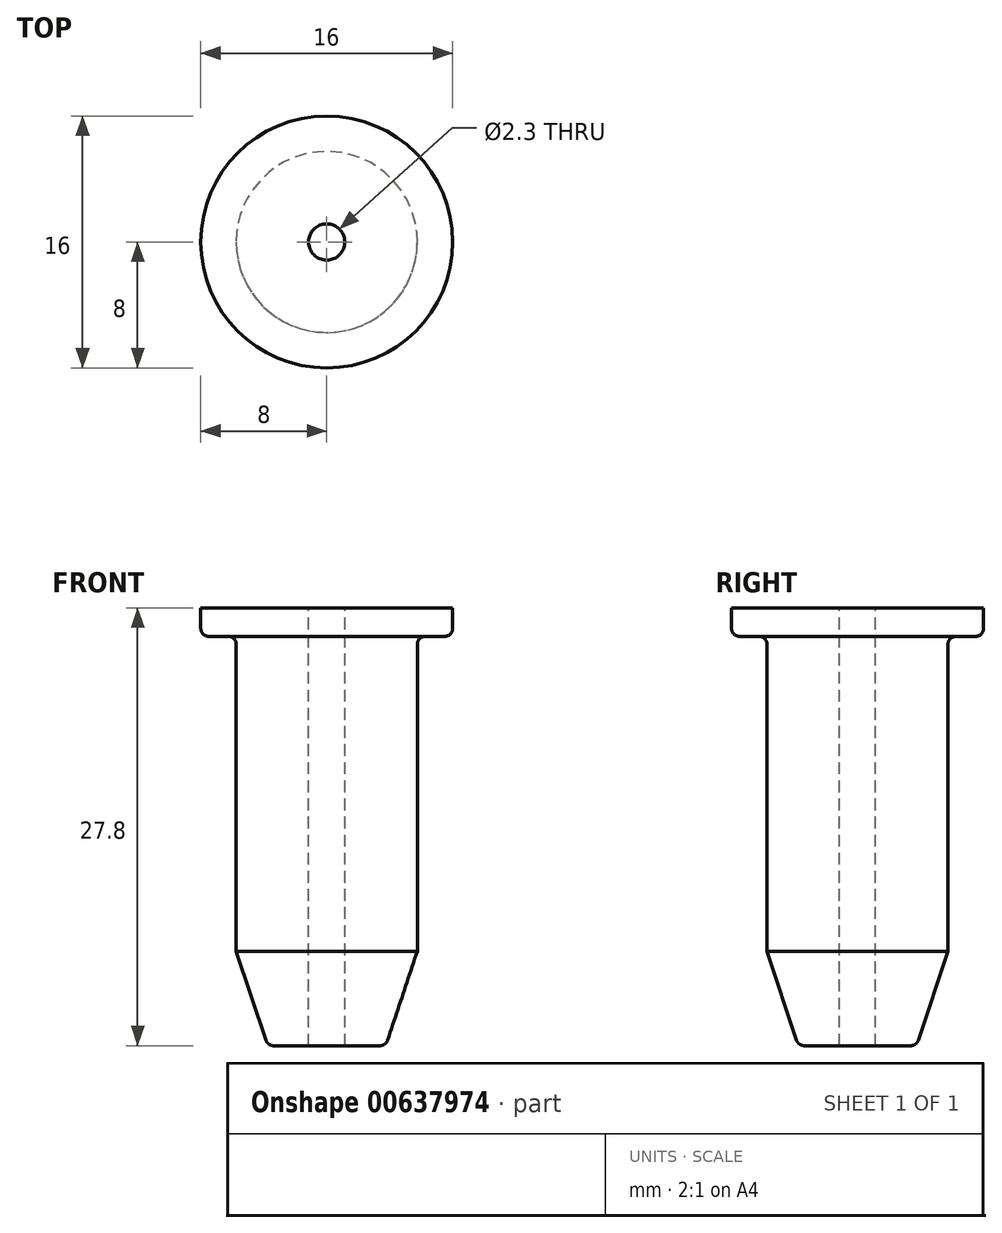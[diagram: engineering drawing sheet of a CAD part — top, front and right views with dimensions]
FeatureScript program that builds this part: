
annotation { "Feature Type Name" : "Feature", "Feature Type Description" : "" }
export const myFeature = defineFeature(function(context is Context, id is Id, definition is map)
    precondition{}
    {
        {
            var Q0;
            Q0=qCreatedBy(makeId("Front.planeOp"),FACE);
            var sketch = newSketch(context, id + "F0", { "sketchPlane" : qUnion([Q0])});
            skLineSegment(sketch, "E0", {"start": v(0, 27.8) * mm, "end": v(8, 27.8) * mm});
            skLineSegment(sketch, "E1", {"start": v(8, 27.8) * mm, "end": v(8, 26) * mm});
            skLineSegment(sketch, "E2", {"start": v(8, 26) * mm, "end": v(5.75, 26) * mm});
            skLineSegment(sketch, "E3", {"start": v(5.75, 26) * mm, "end": v(5.75, 0) * mm});
            skLineSegment(sketch, "E4", {"start": v(0, 27.8) * mm, "end": v(0, 0) * mm});
            skLineSegment(sketch, "E5", {"start": v(0, 0) * mm, "end": v(5.75, 0) * mm});
            skSolve(sketch);
        }
        {
            var Q0;
            Q0=makeQuery(id+"F0.imprint","IMPRINT",FACE,{"disambiguationData":[TD([[makeQuery(id+"F0.imprint","IMPRINT",EDGE,{"derivedFrom":sQuery(id+"F0.wireOp",EDGE,"E0")}),-1.0]])]});
            var Q1;
            Q1=sQuery(id+"F0.wireOp",EDGE,"E4");
            revolve(context, id + "F1", {"entities" : qUnion([Q0]), "axis" : qUnion([Q1]), "revolveType" : RevolveType.FULL});
        }
        {
            var Q0;
            Q0=makeQuery(id+"F1.opRevolve","SWEPT_EDGE",EDGE,{"disambiguationData":[OSD([sQuery(id+"F0.wireOp",EDGE,"E2"),sQuery(id+"F0.wireOp",EDGE,"E3")])]});
            fillet(context, id + "F2", {"entities" : qUnion([Q0]), "radius" : .5 * mm, "tangentPropagation" : true, "allowEdgeOverflow" : false});
        }
        {
            var Q0;
            Q0=makeQuery(id+"F1.opRevolve","SWEPT_EDGE",EDGE,{"disambiguationData":[OSD([sQuery(id+"F0.wireOp",EDGE,"E3"),sQuery(id+"F0.wireOp",EDGE,"E5")])]});
            chamfer(context, id + "F3", {"entities" : qUnion([Q0]), "chamferType" : ChamferType.TWO_OFFSETS, "width1" : 6 * mm, "oppositeDirection" : false, "width2" : 2 * mm, "tangentPropagation" : true});
        }
        {
            var Q0;
            {var subQ0=sQuery(id+"F0.wireOp",EDGE,"E5");Q0=makeQuery(id+"F3.opChamfer","BLEND_EDGE",EDGE,{"blendedFrom":[makeQuery(id+"F1.opRevolve","SWEPT_EDGE",EDGE,{"disambiguationData":[OSD([sQuery(id+"F0.wireOp",EDGE,"E3"),subQ0])]}),makeQuery(id+"F1.opRevolve","SWEPT_FACE",FACE,{"disambiguationData":[OSD([subQ0])]})],"blendedInto":[makeQuery(id+"F1.opRevolve","SWEPT_FACE",FACE,{"disambiguationData":[OSD([subQ0])]})]});}
            fillet(context, id + "F4", {"entities" : qUnion([Q0]), "radius" : .5 * mm, "tangentPropagation" : true, "allowEdgeOverflow" : false});
        }
        {
            var Q0;
            Q0=makeQuery(id+"F1.opRevolve","SWEPT_FACE",FACE,{"disambiguationData":[OSD([sQuery(id+"F0.wireOp",EDGE,"E0")])]});
            var sketch = newSketch(context, id + "F5", { "sketchPlane" : qUnion([Q0])});
            skPoint(sketch, "E6", {"position": v(0, 0) * mm});
            skSolve(sketch);
        }
        {
            var Q0;
            Q0=sQuery(id+"F5.wireOp",VERTEX,"E6");
            var Q1;
            Q1=makeQuery(id+"F1.opRevolve","SWEPT_BODY",BODY,{"disambiguationData":[OSD([sQuery(id+"F0.wireOp",EDGE,"E0"),sQuery(id+"F0.wireOp",EDGE,"E1"),sQuery(id+"F0.wireOp",EDGE,"E2"),sQuery(id+"F0.wireOp",EDGE,"E3"),sQuery(id+"F0.wireOp",EDGE,"E4"),sQuery(id+"F0.wireOp",EDGE,"E5")])]});
            hole(context, id + "F6", {"style" : HoleStyle.SIMPLE, "endStyle" : HoleEndStyle.THROUGH, "holeDiameter" : 2.3 * mm, "majorDiameter" : 5 * mm, "isTappedThrough" : true, "tappedDepth" : 12 * mm, "tapClearance" : 3, "locations" : qUnion([Q0]), "scope" : qUnion([Q1])});
        }
        {
            var Q0;
            Q0=makeQuery(id+"F1.opRevolve","SWEPT_EDGE",EDGE,{"disambiguationData":[OSD([sQuery(id+"F0.wireOp",EDGE,"E1"),sQuery(id+"F0.wireOp",EDGE,"E2")])]});
            fillet(context, id + "F7", {"entities" : qUnion([Q0]), "radius" : .5 * mm, "tangentPropagation" : true, "allowEdgeOverflow" : false});
        }
    });
